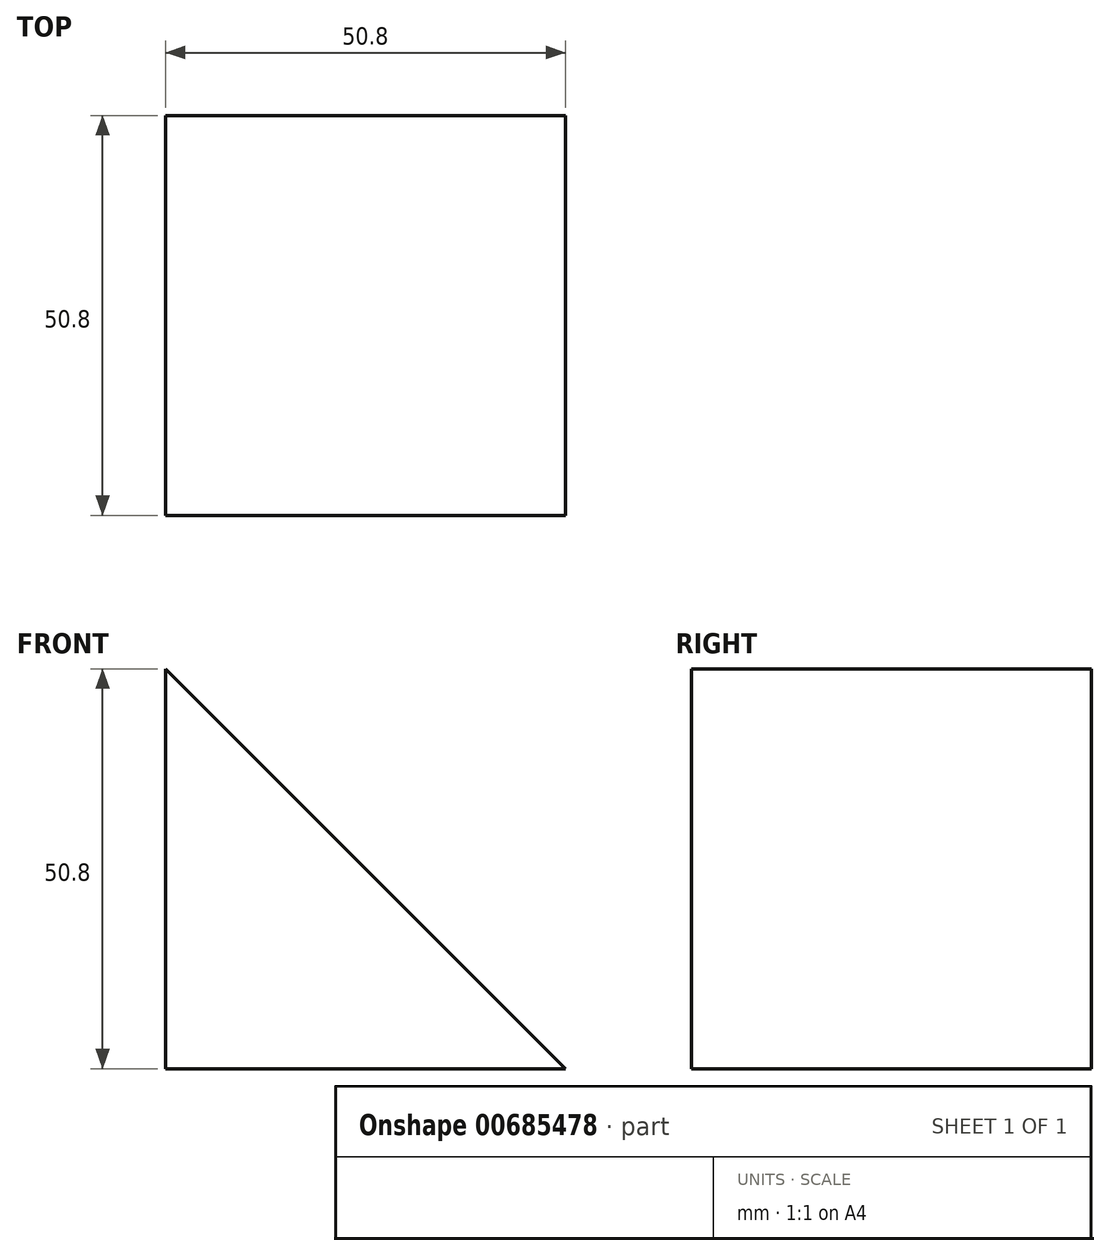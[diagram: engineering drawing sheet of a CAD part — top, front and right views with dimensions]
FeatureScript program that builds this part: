
annotation { "Feature Type Name" : "Feature", "Feature Type Description" : "" }
export const myFeature = defineFeature(function(context is Context, id is Id, definition is map)
    precondition{}
    {
        {
            var Q0;
            Q0=qCreatedBy(makeId("Front.planeOp"),FACE);
            var sketch = newSketch(context, id + "F0", { "sketchPlane" : qUnion([Q0])});
            skLineSegment(sketch, "E0", {"start": v(0, 0) * mm, "end": v(-50.8, 0) * mm});
            skLineSegment(sketch, "E1", {"start": v(-50.8, 0) * mm, "end": v(-50.8, 50.8) * mm});
            skLineSegment(sketch, "E2", {"start": v(-50.8, 50.8) * mm, "end": v(0, 0) * mm});
            skSolve(sketch);
        }
        {
            var Q0;
            Q0 = qSketchRegion(id + "F0", true);
            var Q1;
            Q1=makeQuery(id+"F0.imprint","IMPRINT",FACE,{"disambiguationData":[TD([[makeQuery(id+"F0.imprint","IMPRINT",EDGE,{"derivedFrom":sQuery(id+"F0.wireOp",EDGE,"E0")}),-1.0]])]});
            extrude(context, id + "F1", {"entities" : qUnion([Q0, Q1]), "depth" : 50.8 * mm, "offsetDistance" : 25.4 * mm});
        }
    });
